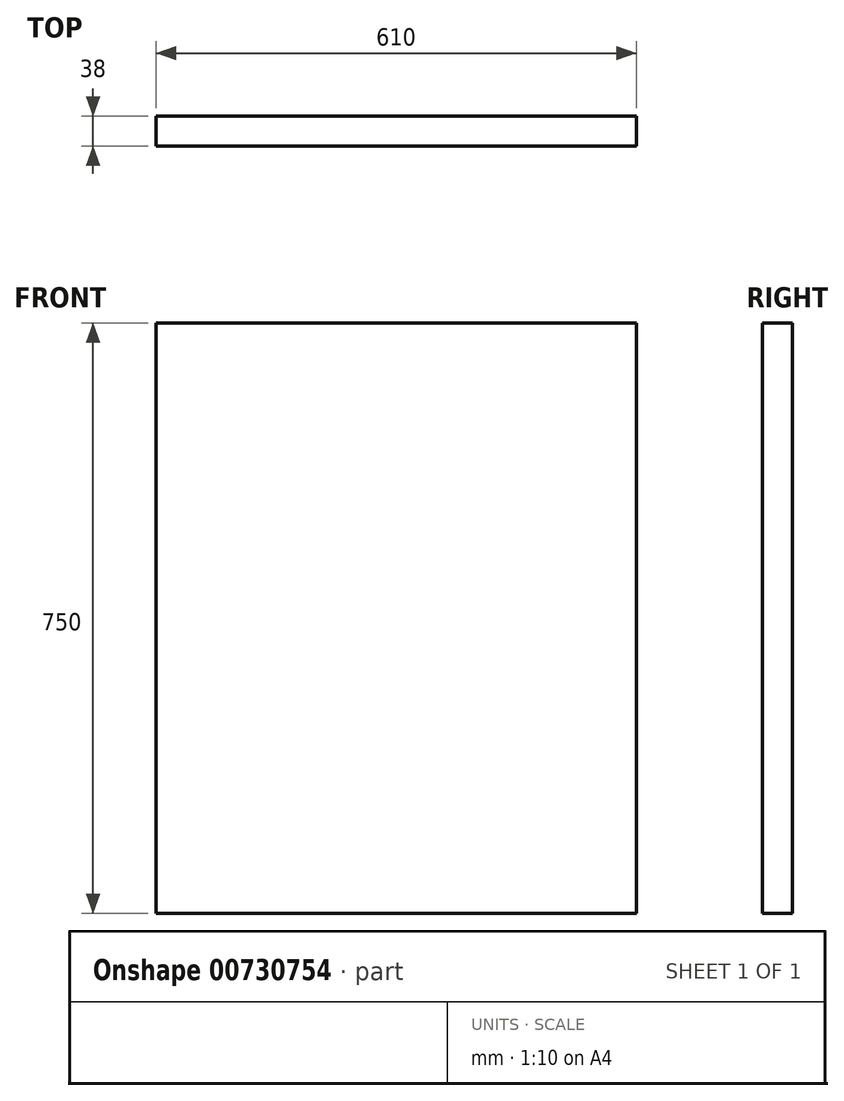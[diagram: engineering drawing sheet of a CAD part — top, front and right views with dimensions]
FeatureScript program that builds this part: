
annotation { "Feature Type Name" : "Feature", "Feature Type Description" : "" }
export const myFeature = defineFeature(function(context is Context, id is Id, definition is map)
    precondition{}
    {
        {
            var Q0;
            Q0=qCreatedBy(makeId("Front.planeOp"),FACE);
            var sketch = newSketch(context, id + "F0", { "sketchPlane" : qUnion([Q0])});
            skLineSegment(sketch, "E0.bottom", {"start": v(-296.89, 375) * mm, "end": v(313.11, 375) * mm});
            skLineSegment(sketch, "E0.top", {"start": v(-296.89, -375) * mm, "end": v(313.11, -375) * mm});
            skLineSegment(sketch, "E0.left", {"start": v(-296.89, 375) * mm, "end": v(-296.89, -375) * mm});
            skLineSegment(sketch, "E0.right", {"start": v(313.11, 375) * mm, "end": v(313.11, -375) * mm});
            skPoint(sketch, "E0.middle", {"position": v(8.11, 0) * mm});
            skSolve(sketch);
        }
        {
            var Q0;
            Q0 = qSketchRegion(id + "F0", true);
            extrude(context, id + "F1", {"entities" : qUnion([Q0]), "endBound" : BoundingType.SYMMETRIC, "depth" : 38 * mm, "offsetDistance" : 25.4 * mm});
        }
    });
